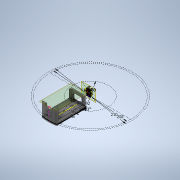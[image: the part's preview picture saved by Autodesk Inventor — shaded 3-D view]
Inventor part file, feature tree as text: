
AUTODESK INVENTOR PART (.ipt)
format: ipt  version: 2020 (Build 240168000, 168)  size: 728,064 bytes
history: native  units: mm
features: projected_geometry x31, extrude x18, sketch x12, fillet x10, other x7, chamfer x2
ambient origin geometry x8: Origin, YZ Plane, XZ Plane, XY Plane, X Axis, Y Axis, Z Axis, Center Point
bodies: Body1 (feature_tree)
feature tree (80):
  other  "Твердое тело1"
  sketch  "Эскиз1"
  extrude  "Выдавливание3"  Depth=202.0mm
  other  "РабПлоскость1"
  extrude  "Выдавливание1"  Depth=35.0mm
  other  "РабПлоскость2"
  sketch  "Эскиз2"
  extrude  "Выдавливание4"  Depth=68.0mm
  extrude  "Выдавливание5"  Depth=2.0mm
  sketch  "Эскиз4"
  extrude  "Выдавливание6"  Depth=2.0mm
  extrude  "Выдавливание7"  Depth=3.0mm
  other  "РабПлоскость3"
  extrude  "Выдавливание8"  Depth=3.0mm
  other  "РабПлоскость4"
  extrude  "Выдавливание9"  Depth=210.0mm
  sketch  "Эскиз8"
  extrude  "Выдавливание10"  Depth=20.0mm TaperAngle=0.0deg
  fillet  "Сопряжение1"  Radius=1.5mm
  fillet  "Сопряжение2"  Radius=28.0mm
  fillet  "Сопряжение3"  Radius=7.0mm
  fillet  "Сопряжение4"  Radius=20.0mm
  fillet  "Сопряжение5"  Radius=13.0mm
  extrude  "Выдавливание11"  Depth=5.0mm
  extrude  "Выдавливание12"  Depth=3.0mm
  fillet  "Сопряжение6"  Radius=10.0mm
  extrude  "Выдавливание13"  Depth=84.0mm
  chamfer  "Фаска1"  Distance=5.0mm
  fillet  "Сопряжение7"  Radius=52.0mm
  sketch  "Эскиз10"
  other  "РабПлоскость5"
  extrude  "Выдавливание14"  Depth=5.0mm TaperAngle=0.0deg
  fillet  "Сопряжение8"  Radius=35.0mm
  extrude  "Выдавливание15"  Depth=18.0mm
  fillet  "Сопряжение9"  Radius=3.0mm
  extrude  "Выдавливание16"  Depth=30.0mm TaperAngle=360.0deg
  fillet  "Сопряжение10"  Radius=0.5mm
  extrude  "Выдавливание17"  TaperAngle=0.0deg  [1 undecoded]
  chamfer  "Фаска2"  Distance=8.0mm
  other  "РабПлоскость7"
  sketch  "Эскиз13"
  extrude  "Выдавливание18"  Depth=2.0mm
  extrude  "Выдавливание19"  Depth=1.5mm TaperAngle=0.0deg
  projected_geometry  "Спроецированная петля1"
  projected_geometry  "Спроецированная петля7"
  projected_geometry  "Спроецированная петля8"
  sketch  "Эскиз3"
  projected_geometry  "Спроецированная петля9"
  projected_geometry  "Спроецированная петля10"
  projected_geometry  "Спроецированная петля11"
  projected_geometry  "Спроецированная петля12"
  sketch  "Эскиз5"
  projected_geometry  "Спроецированная петля13"
  projected_geometry  "Спроецированная петля14"
  projected_geometry  "Спроецированная петля15"
  projected_geometry  "Спроецированная петля16"
  projected_geometry  "Спроецированная петля17"
  sketch  "Эскиз6"
  projected_geometry  "Спроецированная петля18"
  projected_geometry  "Спроецированная петля19"
  projected_geometry  "Спроецированная петля20"
  projected_geometry  "Спроецированная петля21"
  projected_geometry  "Спроецированная петля22"
  projected_geometry  "Спроецированная петля23"
  projected_geometry  "Спроецированная петля24"
  projected_geometry  "Спроецированная петля25"
  projected_geometry  "Спроецированная петля26"
  projected_geometry  "Спроецированная петля27"
  projected_geometry  "Спроецированная петля28"
  sketch  "Эскиз9"
  projected_geometry  "Спроецированная петля29"
  projected_geometry  "Спроецированная петля30"
  sketch  "Эскиз11"
  projected_geometry  "Спроецированная петля31"
  projected_geometry  "Спроецированная петля32"
  projected_geometry  "Спроецированная петля33"
  sketch  "Эскиз12"
  projected_geometry  "Спроецированная петля34"
  projected_geometry  "Спроецированная петля35"
  projected_geometry  "Спроецированная петля36"
note: 1 required parameter value undecoded (feature->parameter linkage not recoverable at this tier; creation-order binding heuristic only, values carry confidence <= 0.55)
